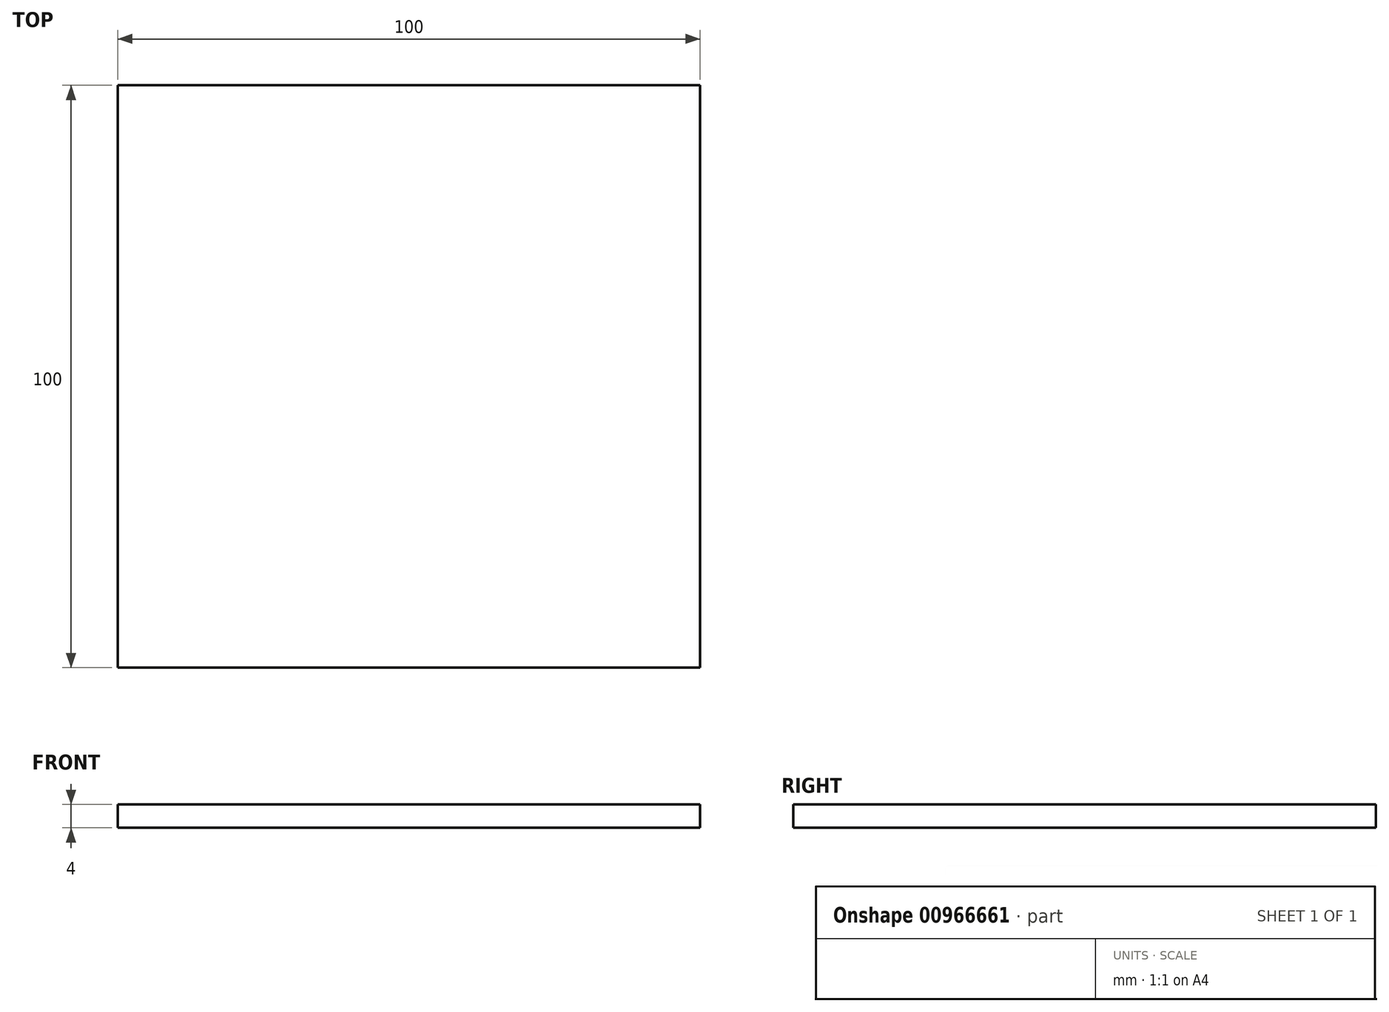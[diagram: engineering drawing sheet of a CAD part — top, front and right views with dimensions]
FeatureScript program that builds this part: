
annotation { "Feature Type Name" : "Feature", "Feature Type Description" : "" }
export const myFeature = defineFeature(function(context is Context, id is Id, definition is map)
    precondition{}
    {
        {
            var Q0;
            Q0=qCreatedBy(makeId("Top.planeOp"),FACE);
            var sketch = newSketch(context, id + "F0", { "sketchPlane" : qUnion([Q0])});
            skLineSegment(sketch, "E0.bottom", {"start": v(50, -50) * mm, "end": v(-50, -50) * mm});
            skLineSegment(sketch, "E0.top", {"start": v(50, 50) * mm, "end": v(-50, 50) * mm});
            skLineSegment(sketch, "E0.left", {"start": v(50, -50) * mm, "end": v(50, 50) * mm});
            skLineSegment(sketch, "E0.right", {"start": v(-50, -50) * mm, "end": v(-50, 50) * mm});
            skPoint(sketch, "E0.middle", {"position": v(0, 0) * mm});
            skSolve(sketch);
        }
        {
            var Q0;
            Q0 = qSketchRegion(id + "F0", true);
            extrude(context, id + "F1", {"entities" : qUnion([Q0]), "depth" : 4 * mm, "offsetDistance" : 25 * mm});
        }
    });
